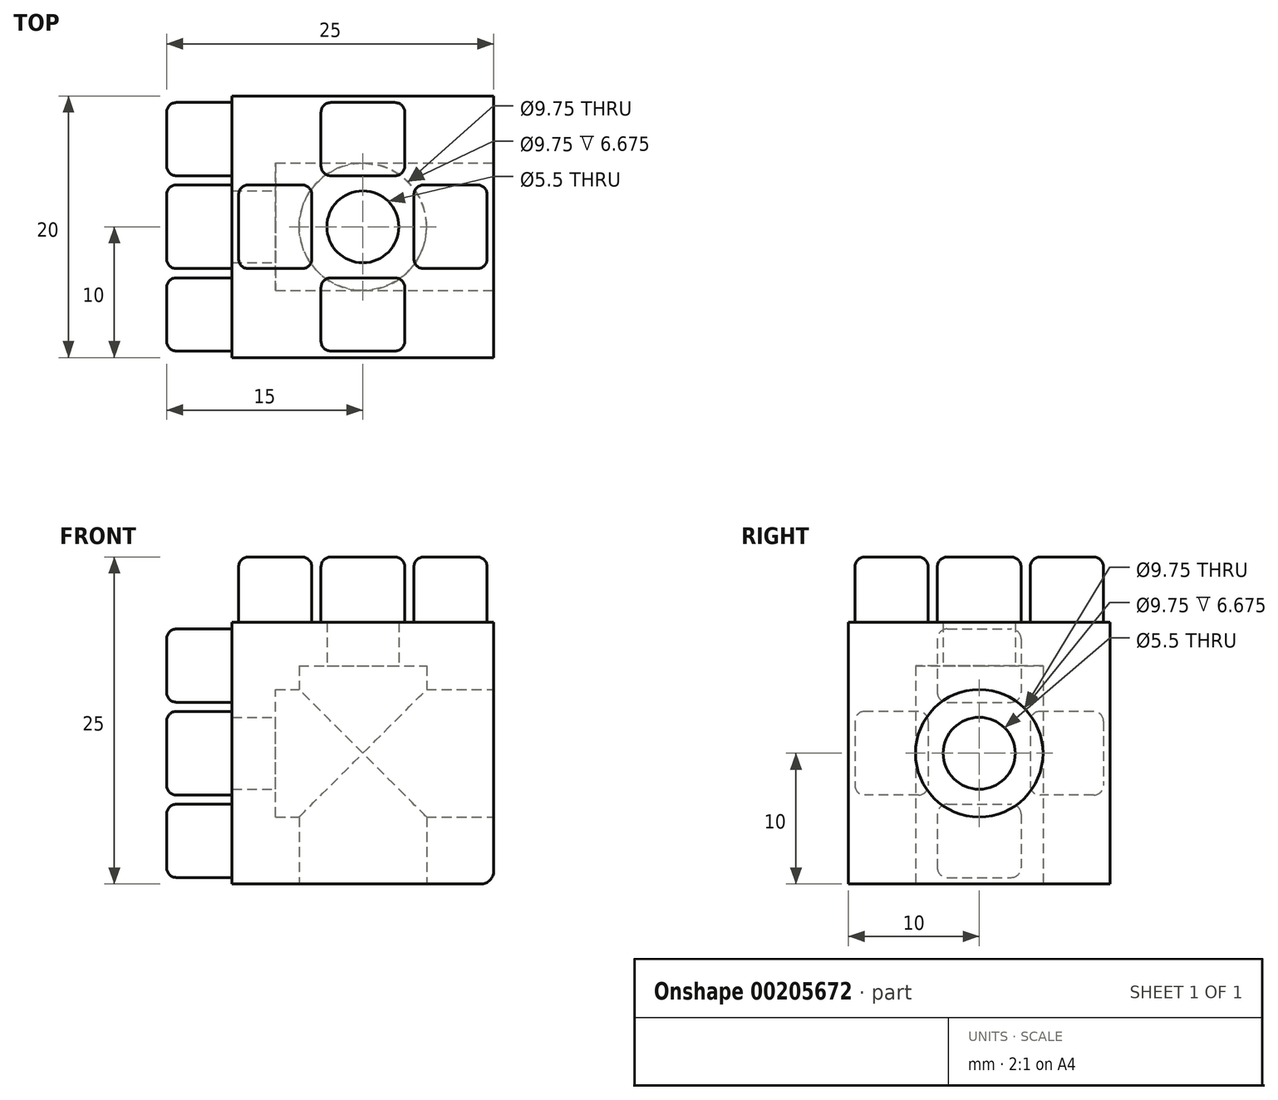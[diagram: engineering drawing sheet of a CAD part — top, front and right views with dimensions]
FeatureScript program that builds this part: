
annotation { "Feature Type Name" : "Feature", "Feature Type Description" : "" }
export const myFeature = defineFeature(function(context is Context, id is Id, definition is map)
    precondition{}
    {
        {
            assignVariable(context, id + "F0", {"name" : "cut_depth", "anyValue" : (10 + 9.75 / 2)});
        }
        {
            var Q0;
            Q0=qCreatedBy(makeId("Top.planeOp"),FACE);
            var sketch = newSketch(context, id + "F1", { "sketchPlane" : qUnion([Q0])});
            skLineSegment(sketch, "E0.bottom", {"start": v(10, 10) * mm, "end": v(-10, 10) * mm});
            skLineSegment(sketch, "E0.top", {"start": v(10, -10) * mm, "end": v(-10, -10) * mm});
            skLineSegment(sketch, "E0.left", {"start": v(10, 10) * mm, "end": v(10, -10) * mm});
            skLineSegment(sketch, "E0.right", {"start": v(-10, 10) * mm, "end": v(-10, -10) * mm});
            skPoint(sketch, "E0.middle", {"position": v(0, 0) * mm});
            skSolve(sketch);
        }
        {
            var Q0;
            Q0=makeQuery(id+"F1.imprint","IMPRINT",FACE,{"disambiguationData":[TD([[makeQuery(id+"F1.imprint","IMPRINT",EDGE,{"derivedFrom":sQuery(id+"F1.wireOp",EDGE,"E0.bottom")}),1.0]])]});
            extrude(context, id + "F2", {"entities" : qUnion([Q0]), "depth" : 20 * mm});
        }
        {
            var Q0;
            Q0=makeQuery(id+"F2.opExtrude","CAP_FACE",FACE,{"disambiguationData":[OSD([sQuery(id+"F1.wireOp",EDGE,"E0.bottom"),sQuery(id+"F1.wireOp",EDGE,"E0.top"),sQuery(id+"F1.wireOp",EDGE,"E0.left"),sQuery(id+"F1.wireOp",EDGE,"E0.right")])],"isStart":false});
            var sketch = newSketch(context, id + "F3", { "sketchPlane" : qUnion([Q0])});
            skLineSegment(sketch, "E1.bottom", {"start": v(-3.9, -3.2) * mm, "end": v(-9.5, -3.2) * mm});
            skLineSegment(sketch, "E1.top", {"start": v(-3.9, 3.2) * mm, "end": v(-9.5, 3.2) * mm});
            skLineSegment(sketch, "E1.left", {"start": v(-3.9, -3.2) * mm, "end": v(-3.9, 3.2) * mm});
            skLineSegment(sketch, "E1.right", {"start": v(-9.5, -3.2) * mm, "end": v(-9.5, 3.2) * mm});
            skPoint(sketch, "E1.middle", {"position": v(-6.7, 0) * mm});
            skLineSegment(sketch, "E2.bottom", {"start": v(9.5, -3.2) * mm, "end": v(3.9, -3.2) * mm});
            skLineSegment(sketch, "E2.top", {"start": v(9.5, 3.2) * mm, "end": v(3.9, 3.2) * mm});
            skLineSegment(sketch, "E2.left", {"start": v(9.5, -3.2) * mm, "end": v(9.5, 3.2) * mm});
            skLineSegment(sketch, "E2.right", {"start": v(3.9, -3.2) * mm, "end": v(3.9, 3.2) * mm});
            skPoint(sketch, "E2.middle", {"position": v(6.7, 0) * mm});
            skLineSegment(sketch, "E3.bottom", {"start": v(3.2, 9.5) * mm, "end": v(-3.2, 9.5) * mm});
            skLineSegment(sketch, "E3.top", {"start": v(3.2, 3.9) * mm, "end": v(-3.2, 3.9) * mm});
            skLineSegment(sketch, "E3.left", {"start": v(3.2, 9.5) * mm, "end": v(3.2, 3.9) * mm});
            skLineSegment(sketch, "E3.right", {"start": v(-3.2, 9.5) * mm, "end": v(-3.2, 3.9) * mm});
            skPoint(sketch, "E3.middle", {"position": v(0, 6.7) * mm});
            skLineSegment(sketch, "E4.bottom", {"start": v(3.2, -3.9) * mm, "end": v(-3.2, -3.9) * mm});
            skLineSegment(sketch, "E4.top", {"start": v(3.2, -9.5) * mm, "end": v(-3.2, -9.5) * mm});
            skLineSegment(sketch, "E4.left", {"start": v(3.2, -3.9) * mm, "end": v(3.2, -9.5) * mm});
            skLineSegment(sketch, "E4.right", {"start": v(-3.2, -3.9) * mm, "end": v(-3.2, -9.5) * mm});
            skPoint(sketch, "E4.middle", {"position": v(0, -6.7) * mm});
            skLineSegment(sketch, "E5.bottom", {"start": v(6.7, -6.7) * mm, "end": v(-6.7, -6.7) * mm, "construction": true});
            skLineSegment(sketch, "E5.top", {"start": v(6.7, 6.7) * mm, "end": v(-6.7, 6.7) * mm, "construction": true});
            skLineSegment(sketch, "E5.left", {"start": v(6.7, -6.7) * mm, "end": v(6.7, 6.7) * mm, "construction": true});
            skLineSegment(sketch, "E5.right", {"start": v(-6.7, -6.7) * mm, "end": v(-6.7, 6.7) * mm, "construction": true});
            skPoint(sketch, "E5.middle", {"position": v(0, 0) * mm});
            skLineSegment(sketch, "E6.bottom", {"start": v(3.9, 3.9) * mm, "end": v(-3.9, 3.9) * mm, "construction": true});
            skLineSegment(sketch, "E6.top", {"start": v(3.9, -3.9) * mm, "end": v(-3.9, -3.9) * mm, "construction": true});
            skLineSegment(sketch, "E6.left", {"start": v(3.9, 3.9) * mm, "end": v(3.9, -3.9) * mm, "construction": true});
            skLineSegment(sketch, "E6.right", {"start": v(-3.9, 3.9) * mm, "end": v(-3.9, -3.9) * mm, "construction": true});
            skSolve(sketch);
        }
        {
            var Q0;
            Q0=makeQuery(id+"F3.imprint","IMPRINT",FACE,{"disambiguationData":[TD([[makeQuery(id+"F3.imprint","IMPRINT",EDGE,{"derivedFrom":sQuery(id+"F3.wireOp",EDGE,"E3.bottom")}),1.0]])]});
            var Q1;
            Q1=makeQuery(id+"F3.imprint","IMPRINT",FACE,{"disambiguationData":[TD([[makeQuery(id+"F3.imprint","IMPRINT",EDGE,{"derivedFrom":sQuery(id+"F3.wireOp",EDGE,"E1.bottom")}),-1.0]])]});
            var Q2;
            Q2=makeQuery(id+"F3.imprint","IMPRINT",FACE,{"disambiguationData":[TD([[makeQuery(id+"F3.imprint","IMPRINT",EDGE,{"derivedFrom":sQuery(id+"F3.wireOp",EDGE,"E4.bottom")}),1.0]])]});
            var Q3;
            Q3=makeQuery(id+"F3.imprint","IMPRINT",FACE,{"disambiguationData":[TD([[makeQuery(id+"F3.imprint","IMPRINT",EDGE,{"derivedFrom":sQuery(id+"F3.wireOp",EDGE,"E2.bottom")}),-1.0]])]});
            extrude(context, id + "F4", {"entities" : qUnion([Q0, Q1, Q2, Q3]), "depth" : 5 * mm});
        }
        {
            var Q0;
            Q0=makeQuery(id+"F2.opExtrude","SWEPT_EDGE",EDGE,{"disambiguationData":[OSD([sQuery(id+"F1.wireOp",EDGE,"E0.top"),sQuery(id+"F1.wireOp",EDGE,"E0.right")])]});
            cPoint(context, id + "F5", {"entities" : qUnion([Q0]), "parameter" : 0.5});
        }
        {
            var Q0;
            Q0=makeQuery(id+"F2.opExtrude","SWEPT_EDGE",EDGE,{"disambiguationData":[OSD([sQuery(id+"F1.wireOp",EDGE,"E0.bottom"),sQuery(id+"F1.wireOp",EDGE,"E0.right")])]});
            cPoint(context, id + "F6", {"entities" : qUnion([Q0]), "parameter" : 0.5});
        }
        {
            var Q0;
            Q0=makeQuery(id+"F2.opExtrude","SWEPT_EDGE",EDGE,{"disambiguationData":[OSD([sQuery(id+"F1.wireOp",EDGE,"E0.bottom"),sQuery(id+"F1.wireOp",EDGE,"E0.left")])]});
            cPoint(context, id + "F7", {"entities" : qUnion([Q0]), "parameter" : 0.5});
        }
        {
            var Q0;
            Q0=qCreatedBy(id+"F5",VERTEX);
            var Q1;
            Q1=qCreatedBy(id+"F6",VERTEX);
            var Q2;
            Q2=qCreatedBy(id+"F7",VERTEX);
            cPlane(context, id + "F8", {"entities" : qUnion([Q0, Q1, Q2]), "cplaneType" : CPlaneType.THREE_POINT, "offset" : 25 * mm, "width" : 150 * mm, "height" : 150 * mm});
        }
        {
            var Q0;
            Q0=qCreatedBy(id+"F8.planeOp",FACE);
            var sketch = newSketch(context, id + "F9", { "sketchPlane" : qUnion([Q0])});
            skPoint(sketch, "E7.0", {"position": v(-10, 0) * mm});
            skPoint(sketch, "E8.0", {"position": v(0, 10) * mm});
            skPoint(sketch, "E9.0", {"position": v(10, 0) * mm});
            skPoint(sketch, "E10.0", {"position": v(0, -10) * mm});
            skLineSegment(sketch, "E11", {"start": v(-10, 0) * mm, "end": v(10, 0) * mm, "construction": true});
            skLineSegment(sketch, "E12", {"start": v(0, 10) * mm, "end": v(0, -10) * mm, "construction": true});
            skSolve(sketch);
        }
        {
            var Q0;
            Q0=makeQuery(id+"F4.opExtrude","SWEPT_EDGE",EDGE,{"disambiguationData":[OSD([sQuery(id+"F3.wireOp",EDGE,"E2.top"),sQuery(id+"F3.wireOp",EDGE,"E2.left")])]});
            var Q1;
            Q1=makeQuery(id+"F4.opExtrude","SWEPT_EDGE",EDGE,{"disambiguationData":[OSD([sQuery(id+"F3.wireOp",EDGE,"E2.top"),sQuery(id+"F3.wireOp",EDGE,"E2.right")])]});
            var Q2;
            Q2=makeQuery(id+"F4.opExtrude","SWEPT_EDGE",EDGE,{"disambiguationData":[OSD([sQuery(id+"F3.wireOp",EDGE,"E3.top"),sQuery(id+"F3.wireOp",EDGE,"E3.left")])]});
            var Q3;
            Q3=makeQuery(id+"F4.opExtrude","SWEPT_EDGE",EDGE,{"disambiguationData":[OSD([sQuery(id+"F3.wireOp",EDGE,"E3.bottom"),sQuery(id+"F3.wireOp",EDGE,"E3.left")])]});
            var Q4;
            Q4=makeQuery(id+"F4.opExtrude","SWEPT_EDGE",EDGE,{"disambiguationData":[OSD([sQuery(id+"F3.wireOp",EDGE,"E3.bottom"),sQuery(id+"F3.wireOp",EDGE,"E3.right")])]});
            var Q5;
            Q5=makeQuery(id+"F4.opExtrude","SWEPT_EDGE",EDGE,{"disambiguationData":[OSD([sQuery(id+"F3.wireOp",EDGE,"E2.bottom"),sQuery(id+"F3.wireOp",EDGE,"E2.left")])]});
            var Q6;
            Q6=makeQuery(id+"F4.opExtrude","SWEPT_EDGE",EDGE,{"disambiguationData":[OSD([sQuery(id+"F3.wireOp",EDGE,"E4.top"),sQuery(id+"F3.wireOp",EDGE,"E4.left")])]});
            var Q7;
            Q7=makeQuery(id+"F4.opExtrude","SWEPT_EDGE",EDGE,{"disambiguationData":[OSD([sQuery(id+"F3.wireOp",EDGE,"E4.bottom"),sQuery(id+"F3.wireOp",EDGE,"E4.right")])]});
            var Q8;
            Q8=makeQuery(id+"F4.opExtrude","SWEPT_EDGE",EDGE,{"disambiguationData":[OSD([sQuery(id+"F3.wireOp",EDGE,"E1.bottom"),sQuery(id+"F3.wireOp",EDGE,"E1.left")])]});
            var Q9;
            Q9=makeQuery(id+"F4.opExtrude","SWEPT_EDGE",EDGE,{"disambiguationData":[OSD([sQuery(id+"F3.wireOp",EDGE,"E1.top"),sQuery(id+"F3.wireOp",EDGE,"E1.right")])]});
            var Q10;
            Q10=makeQuery(id+"F4.opExtrude","SWEPT_EDGE",EDGE,{"disambiguationData":[OSD([sQuery(id+"F3.wireOp",EDGE,"E4.bottom"),sQuery(id+"F3.wireOp",EDGE,"E4.left")])]});
            var Q11;
            Q11=makeQuery(id+"F4.opExtrude","SWEPT_EDGE",EDGE,{"disambiguationData":[OSD([sQuery(id+"F3.wireOp",EDGE,"E1.top"),sQuery(id+"F3.wireOp",EDGE,"E1.left")])]});
            var Q12;
            Q12=makeQuery(id+"F4.opExtrude","SWEPT_EDGE",EDGE,{"disambiguationData":[OSD([sQuery(id+"F3.wireOp",EDGE,"E1.bottom"),sQuery(id+"F3.wireOp",EDGE,"E1.right")])]});
            var Q13;
            Q13=makeQuery(id+"F4.opExtrude","SWEPT_EDGE",EDGE,{"disambiguationData":[OSD([sQuery(id+"F3.wireOp",EDGE,"E3.top"),sQuery(id+"F3.wireOp",EDGE,"E3.right")])]});
            var Q14;
            Q14=makeQuery(id+"F4.opExtrude","SWEPT_EDGE",EDGE,{"disambiguationData":[OSD([sQuery(id+"F3.wireOp",EDGE,"E4.top"),sQuery(id+"F3.wireOp",EDGE,"E4.right")])]});
            var Q15;
            Q15=makeQuery(id+"F4.opExtrude","SWEPT_EDGE",EDGE,{"disambiguationData":[OSD([sQuery(id+"F3.wireOp",EDGE,"E2.bottom"),sQuery(id+"F3.wireOp",EDGE,"E2.right")])]});
            var Q16;
            Q16=makeQuery(id+"F4.opExtrude","CAP_EDGE",EDGE,{"disambiguationData":[OSD([sQuery(id+"F3.wireOp",EDGE,"E2.left")])],"isStart":false});
            var Q17;
            Q17=makeQuery(id+"F4.opExtrude","CAP_EDGE",EDGE,{"disambiguationData":[OSD([sQuery(id+"F3.wireOp",EDGE,"E2.top")])],"isStart":false});
            var Q18;
            Q18=makeQuery(id+"F4.opExtrude","CAP_EDGE",EDGE,{"disambiguationData":[OSD([sQuery(id+"F3.wireOp",EDGE,"E2.bottom")])],"isStart":false});
            var Q19;
            Q19=makeQuery(id+"F4.opExtrude","CAP_EDGE",EDGE,{"disambiguationData":[OSD([sQuery(id+"F3.wireOp",EDGE,"E2.right")])],"isStart":false});
            var Q20;
            Q20=makeQuery(id+"F4.opExtrude","CAP_EDGE",EDGE,{"disambiguationData":[OSD([sQuery(id+"F3.wireOp",EDGE,"E3.left")])],"isStart":false});
            var Q21;
            Q21=makeQuery(id+"F4.opExtrude","CAP_EDGE",EDGE,{"disambiguationData":[OSD([sQuery(id+"F3.wireOp",EDGE,"E3.bottom")])],"isStart":false});
            var Q22;
            Q22=makeQuery(id+"F4.opExtrude","CAP_EDGE",EDGE,{"disambiguationData":[OSD([sQuery(id+"F3.wireOp",EDGE,"E3.top")])],"isStart":false});
            var Q23;
            Q23=makeQuery(id+"F4.opExtrude","CAP_EDGE",EDGE,{"disambiguationData":[OSD([sQuery(id+"F3.wireOp",EDGE,"E1.top")])],"isStart":false});
            var Q24;
            Q24=makeQuery(id+"F4.opExtrude","CAP_EDGE",EDGE,{"disambiguationData":[OSD([sQuery(id+"F3.wireOp",EDGE,"E1.left")])],"isStart":false});
            var Q25;
            Q25=makeQuery(id+"F4.opExtrude","CAP_EDGE",EDGE,{"disambiguationData":[OSD([sQuery(id+"F3.wireOp",EDGE,"E1.right")])],"isStart":false});
            var Q26;
            Q26=makeQuery(id+"F4.opExtrude","CAP_EDGE",EDGE,{"disambiguationData":[OSD([sQuery(id+"F3.wireOp",EDGE,"E1.bottom")])],"isStart":false});
            var Q27;
            Q27=makeQuery(id+"F4.opExtrude","CAP_EDGE",EDGE,{"disambiguationData":[OSD([sQuery(id+"F3.wireOp",EDGE,"E4.bottom")])],"isStart":false});
            var Q28;
            Q28=makeQuery(id+"F4.opExtrude","CAP_EDGE",EDGE,{"disambiguationData":[OSD([sQuery(id+"F3.wireOp",EDGE,"E4.left")])],"isStart":false});
            var Q29;
            Q29=makeQuery(id+"F4.opExtrude","CAP_EDGE",EDGE,{"disambiguationData":[OSD([sQuery(id+"F3.wireOp",EDGE,"E4.top")])],"isStart":false});
            var Q30;
            Q30=makeQuery(id+"F4.opExtrude","CAP_EDGE",EDGE,{"disambiguationData":[OSD([sQuery(id+"F3.wireOp",EDGE,"E4.right")])],"isStart":false});
            var Q31;
            Q31=makeQuery(id+"F4.opExtrude","CAP_EDGE",EDGE,{"disambiguationData":[OSD([sQuery(id+"F3.wireOp",EDGE,"E3.right")])],"isStart":false});
            fillet(context, id + "F10", {"entities" : qUnion([Q0, Q1, Q2, Q3, Q4, Q5, Q6, Q7, Q8, Q9, Q10, Q11, Q12, Q13, Q14, Q15, Q16, Q17, Q18, Q19, Q20, Q21, Q22, Q23, Q24, Q25, Q26, Q27, Q28, Q29, Q30, Q31]), "radius" : 0.75 * mm, "tangentPropagation" : true, "allowEdgeOverflow" : false});
        }
        {
            var Q0;
            Q0=makeQuery(id+"F4.opExtrude","SWEPT_BODY",BODY,{"disambiguationData":[OSD([sQuery(id+"F3.wireOp",EDGE,"E3.bottom"),sQuery(id+"F3.wireOp",EDGE,"E3.top"),sQuery(id+"F3.wireOp",EDGE,"E3.left"),sQuery(id+"F3.wireOp",EDGE,"E3.right")])]});
            var Q1;
            Q1=makeQuery(id+"F4.opExtrude","SWEPT_BODY",BODY,{"disambiguationData":[OSD([sQuery(id+"F3.wireOp",EDGE,"E1.bottom"),sQuery(id+"F3.wireOp",EDGE,"E1.top"),sQuery(id+"F3.wireOp",EDGE,"E1.left"),sQuery(id+"F3.wireOp",EDGE,"E1.right")])]});
            var Q2;
            Q2=makeQuery(id+"F4.opExtrude","SWEPT_BODY",BODY,{"disambiguationData":[OSD([sQuery(id+"F3.wireOp",EDGE,"E2.bottom"),sQuery(id+"F3.wireOp",EDGE,"E2.top"),sQuery(id+"F3.wireOp",EDGE,"E2.left"),sQuery(id+"F3.wireOp",EDGE,"E2.right")])]});
            var Q3;
            Q3=makeQuery(id+"F4.opExtrude","SWEPT_BODY",BODY,{"disambiguationData":[OSD([sQuery(id+"F3.wireOp",EDGE,"E4.bottom"),sQuery(id+"F3.wireOp",EDGE,"E4.top"),sQuery(id+"F3.wireOp",EDGE,"E4.left"),sQuery(id+"F3.wireOp",EDGE,"E4.right")])]});
            var Q4;
            Q4=sQuery(id+"F9.wireOp",EDGE,"E12");
            circularPattern(context, id + "F11", {"operationType" : NewBodyOperationType.ADD, "entities" : qUnion([Q0, Q1, Q2, Q3]), "axis" : qUnion([Q4]), "angle" : 90 * degree, "instanceCount" : 2, "equalSpace" : true});
        }
        {
            var Q0;
            Q0=makeQuery(id+"F2.opExtrude","CAP_FACE",FACE,{"disambiguationData":[OSD([sQuery(id+"F1.wireOp",EDGE,"E0.bottom"),sQuery(id+"F1.wireOp",EDGE,"E0.top"),sQuery(id+"F1.wireOp",EDGE,"E0.left"),sQuery(id+"F1.wireOp",EDGE,"E0.right")])],"isStart":true});
            var sketch = newSketch(context, id + "F12", { "sketchPlane" : qUnion([Q0])});
            skCircle(sketch, "E13", {"center": v(0, 0) * mm, "radius": 4.88 * mm});
            skSolve(sketch);
        }
        {
            var Q0;
            Q0=makeQuery(id+"F2.opExtrude","SWEPT_FACE",FACE,{"disambiguationData":[OSD([sQuery(id+"F1.wireOp",EDGE,"E0.left")])]});
            var sketch = newSketch(context, id + "F13", { "sketchPlane" : qUnion([Q0])});
            skPoint(sketch, "E14.0", {"position": v(0, 10) * mm});
            skCircle(sketch, "E15", {"center": v(0, 10) * mm, "radius": 4.88 * mm});
            skSolve(sketch);
        }
        {
            var Q0;
            Q0=makeQuery(id+"F13.imprint","IMPRINT",FACE,{"disambiguationData":[TD([[makeQuery(id+"F13.imprint","IMPRINT",EDGE,{"derivedFrom":sQuery(id+"F13.wireOp",EDGE,"E15")}),1.0]])]});
            extrude(context, id + "F14", {"entities" : qUnion([Q0]), "operationType" : NewBodyOperationType.REMOVE, "oppositeDirection" : true, "depth" : (getVariable(context, 'cut_depth')) * mm});
        }
        {
            var Q0;
            Q0=makeQuery(id+"F12.imprint","IMPRINT",FACE,{"disambiguationData":[TD([[makeQuery(id+"F12.imprint","IMPRINT",EDGE,{"derivedFrom":sQuery(id+"F12.wireOp",EDGE,"E13")}),1.0]])]});
            extrude(context, id + "F15", {"entities" : qUnion([Q0]), "operationType" : NewBodyOperationType.REMOVE, "oppositeDirection" : true, "depth" : (getVariable(context, 'cut_depth')) * mm});
        }
        {
            var Q0;
            Q0=makeQuery(id+"F14.boolean.opBoolean","COPY",FACE,{"derivedFrom":makeQuery(id+"F14.opExtrude","CAP_FACE",FACE,{"disambiguationData":[OSD([sQuery(id+"F13.wireOp",EDGE,"E15")])],"isStart":false})});
            var sketch = newSketch(context, id + "F16", { "sketchPlane" : qUnion([Q0])});
            skPoint(sketch, "E16.0", {"position": v(0, 10) * mm});
            skSolve(sketch);
        }
        {
            var Q0;
            Q0=makeQuery(id+"F15.boolean.opBoolean","COPY",FACE,{"derivedFrom":makeQuery(id+"F15.opExtrude","CAP_FACE",FACE,{"disambiguationData":[OSD([sQuery(id+"F12.wireOp",EDGE,"E13")])],"isStart":false})});
            var sketch = newSketch(context, id + "F17", { "sketchPlane" : qUnion([Q0])});
            skPoint(sketch, "E17.0", {"position": v(0, 0) * mm});
            skSolve(sketch);
        }
        {
            var Q0;
            Q0=sQuery(id+"F17.wireOp",VERTEX,"E17.0");
            var Q1;
            Q1=sQuery(id+"F16.wireOp",VERTEX,"E16.0");
            var Q2;
            Q2=makeQuery(id+"F2.opExtrude","SWEPT_BODY",BODY,{"disambiguationData":[OSD([sQuery(id+"F1.wireOp",EDGE,"E0.bottom"),sQuery(id+"F1.wireOp",EDGE,"E0.top"),sQuery(id+"F1.wireOp",EDGE,"E0.left"),sQuery(id+"F1.wireOp",EDGE,"E0.right")])]});
            hole(context, id + "F18", {"style" : HoleStyle.C_BORE, "endStyle" : HoleEndStyle.BLIND, "holeDiameter" : 5.5 * mm, "cBoreDiameter" : 9.75 * mm, "cBoreDepth" : 1.8 * mm, "holeDepth" : 20 * mm, "locations" : qUnion([Q0, Q1]), "scope" : qUnion([Q2])});
        }
        {
            var Q0;
            Q0=makeQuery(id+"F2.opExtrude","CAP_EDGE",EDGE,{"disambiguationData":[OSD([sQuery(id+"F1.wireOp",EDGE,"E0.left")])],"isStart":true});
            fillet(context, id + "F19", {"entities" : qUnion([Q0]), "radius" : 1 * mm, "tangentPropagation" : true, "allowEdgeOverflow" : false});
        }
    });
